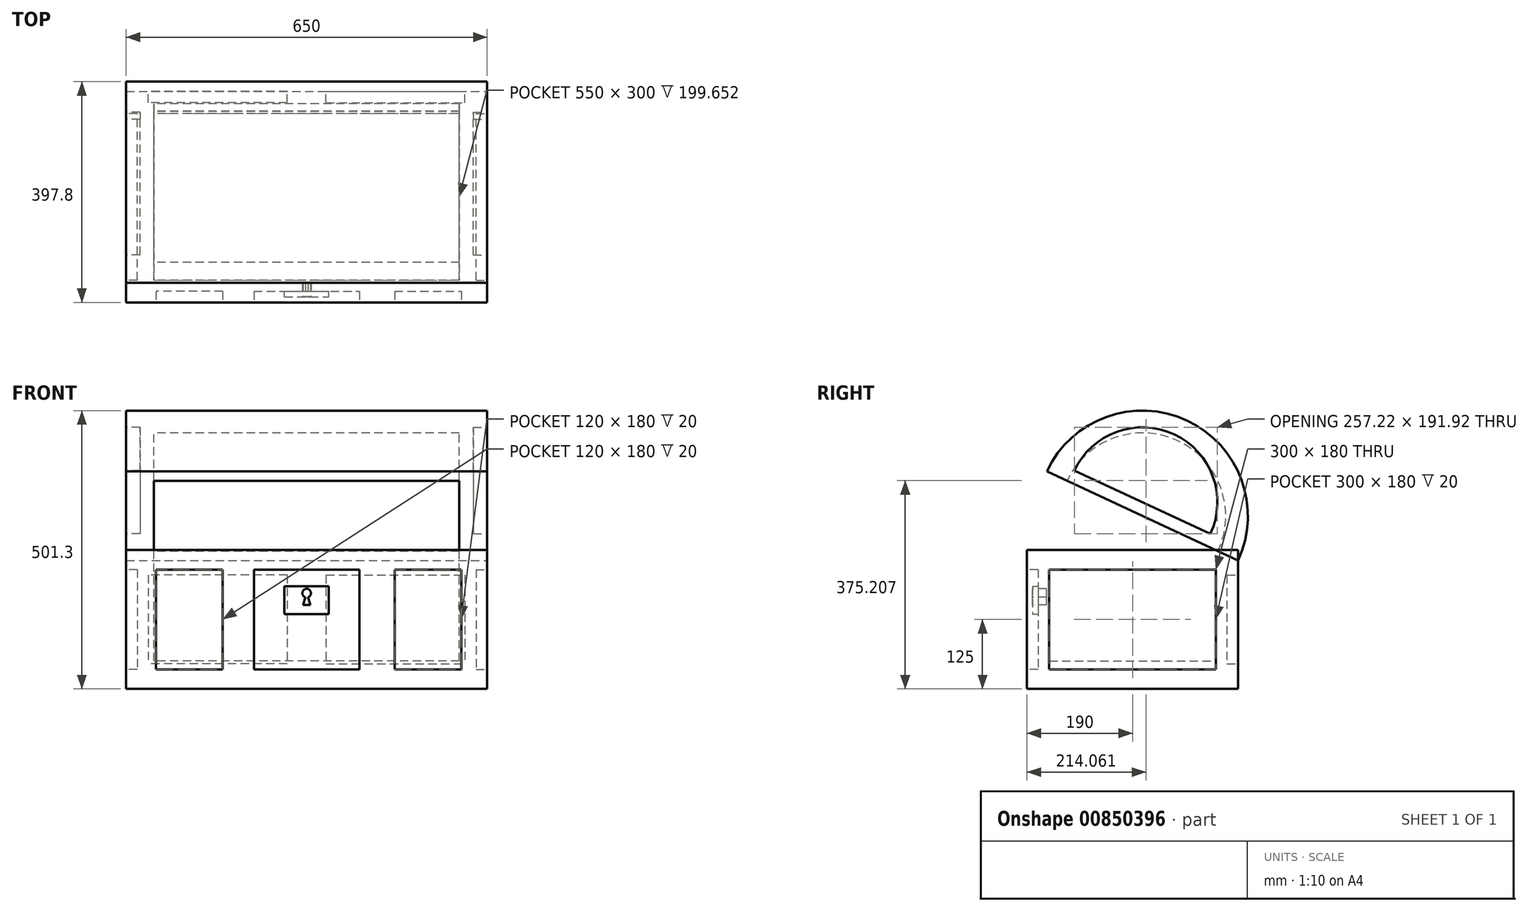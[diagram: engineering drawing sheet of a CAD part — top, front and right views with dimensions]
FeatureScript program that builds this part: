
annotation { "Feature Type Name" : "Feature", "Feature Type Description" : "" }
export const myFeature = defineFeature(function(context is Context, id is Id, definition is map)
    precondition{}
    {
        {
            var Q0;
            Q0=qCreatedBy(makeId("Top.planeOp"),FACE);
            var sketch = newSketch(context, id + "F0", { "sketchPlane" : qUnion([Q0])});
            skLineSegment(sketch, "E0.bottom", {"start": v(-32.5, 19) * mm, "end": v(32.5, 19) * mm});
            skLineSegment(sketch, "E0.top", {"start": v(-32.5, -19) * mm, "end": v(32.5, -19) * mm});
            skLineSegment(sketch, "E0.left", {"start": v(-32.5, 19) * mm, "end": v(-32.5, -19) * mm});
            skLineSegment(sketch, "E0.right", {"start": v(32.5, 19) * mm, "end": v(32.5, -19) * mm});
            skPoint(sketch, "E0.middle", {"position": v(0, 0) * mm});
            skSolve(sketch);
        }
        {
            var Q0;
            Q0=qSketchRegion(id+"F0",true);
            extrude(context, id + "F1", {"entities" : qUnion([Q0]), "depth" : 25 * mm, "offsetDistance" : 25 * mm});
        }
        {
            var Q0;
            Q0=qCreatedBy(makeId("Right.planeOp"),FACE);
            var sketch = newSketch(context, id + "F2", { "sketchPlane" : qUnion([Q0])});
            skArc(sketch, "E1", {"start": v(-19, 23.1) * mm, "mid": v(-9.8, 48.35) * mm, "end": v(15.44, 39.16) * mm});
            skLineSegment(sketch, "E2", {"start": v(15.44, 39.16) * mm, "end": v(-19, 23.1) * mm});
            skSolve(sketch);
        }
        {
            var Q0;
            Q0=qSketchRegion(id+"F2",true);
            extrude(context, id + "F3", {"entities" : qUnion([Q0]), "endBound" : BoundingType.SYMMETRIC, "depth" : 65 * mm, "offsetDistance" : 25 * mm});
        }
        {
            var Q0;
            Q0=qCreatedBy(makeId("Right.planeOp"),FACE);
            var sketch = newSketch(context, id + "F4", { "sketchPlane" : qUnion([Q0])});
            skArc(sketch, "E3", {"start": v(-15.37, 24.8) * mm, "mid": v(-8.12, 44.72) * mm, "end": v(11.81, 37.47) * mm});
            skLineSegment(sketch, "E4", {"start": v(11.81, 37.47) * mm, "end": v(-15.37, 24.8) * mm});
            skSolve(sketch);
        }
        {
            var Q0;
            Q0=qSketchRegion(id+"F4",true);
            extrude(context, id + "F5", {"entities" : qUnion([Q0]), "operationType" : NewBodyOperationType.REMOVE, "endBound" : BoundingType.SYMMETRIC, "oppositeDirection" : true, "depth" : 55 * mm, "offsetDistance" : 25 * mm});
        }
        {
            var Q0;
            Q0=makeQuery(id+"F3.opExtrude","CAP_FACE",FACE,{"disambiguationData":[OSD([sQuery(id+"F2.wireOp",EDGE,"E1"),sQuery(id+"F2.wireOp",EDGE,"E2")])],"isStart":false});
            var sketch = newSketch(context, id + "F6", { "sketchPlane" : qUnion([Q0])});
            skArc(sketch, "E5", {"start": v(-14.02, 25.42) * mm, "mid": v(-7.49, 43.36) * mm, "end": v(10.46, 36.84) * mm});
            skLineSegment(sketch, "E6", {"start": v(-14.02, 25.42) * mm, "end": v(10.46, 36.84) * mm});
            skSolve(sketch);
        }
        {
            var Q0;
            Q0=qSketchRegion(id+"F6",true);
            extrude(context, id + "F7", {"entities" : qUnion([Q0]), "oppositeDirection" : true, "depth" : 2.5 * mm, "offsetDistance" : 25 * mm});
        }
        {
            var Q0;
            Q0=makeQuery(id+"F7.opExtrude","SWEPT_BODY",BODY,{"disambiguationData":[OSD([sQuery(id+"F6.wireOp",EDGE,"E5"),sQuery(id+"F6.wireOp",EDGE,"E6")])]});
            transform(context, id + "F8", {"entities" : qUnion([Q0]), "transformType" : TransformType.TRANSLATION_3D, "dx" : 0 * mm, "dy" : 0 * mm, "dz" : 2.5 * mm, "makeCopy" : false});
        }
        {
            var Q0;
            Q0=makeQuery(id+"F7.opExtrude","SWEPT_BODY",BODY,{"disambiguationData":[OSD([sQuery(id+"F6.wireOp",EDGE,"E5"),sQuery(id+"F6.wireOp",EDGE,"E6")])]});
            var Q1;
            Q1=qCreatedBy(makeId("Right.planeOp"),FACE);
            mirror(context, id + "F9", {"entities" : qUnion([Q0]), "mirrorPlane" : qUnion([Q1])});
        }
        {
            var Q0;
            Q0=makeQuery(id+"F9.opPattern","COPY",BODY,{"derivedFrom":makeQuery(id+"F7.opExtrude","SWEPT_BODY",BODY,{"disambiguationData":[OSD([sQuery(id+"F6.wireOp",EDGE,"E5"),sQuery(id+"F6.wireOp",EDGE,"E6")])]}),"instanceName":"1"});
            var Q1;
            Q1=makeQuery(id+"F7.opExtrude","SWEPT_BODY",BODY,{"disambiguationData":[OSD([sQuery(id+"F6.wireOp",EDGE,"E5"),sQuery(id+"F6.wireOp",EDGE,"E6")])]});
            var Q2;
            Q2=makeQuery(id+"F3.opExtrude","SWEPT_BODY",BODY,{"disambiguationData":[OSD([sQuery(id+"F2.wireOp",EDGE,"E1"),sQuery(id+"F2.wireOp",EDGE,"E2")])]});
            booleanBodies(context, id + "F10", {"operationType" : BooleanOperationType.SUBTRACTION, "tools" : qUnion([Q0, Q1]), "targets" : qUnion([Q2])});
        }
        {
            var Q0;
            Q0=makeQuery(id+"F1.opExtrude","CAP_FACE",FACE,{"disambiguationData":[OSD([sQuery(id+"F0.wireOp",EDGE,"E0.bottom"),sQuery(id+"F0.wireOp",EDGE,"E0.top"),sQuery(id+"F0.wireOp",EDGE,"E0.left"),sQuery(id+"F0.wireOp",EDGE,"E0.right")])],"isStart":false});
            var sketch = newSketch(context, id + "F11", { "sketchPlane" : qUnion([Q0])});
            skLineSegment(sketch, "E7.bottom", {"start": v(-27.5, 15) * mm, "end": v(27.5, 15) * mm});
            skLineSegment(sketch, "E7.top", {"start": v(-27.5, -15) * mm, "end": v(27.5, -15) * mm});
            skLineSegment(sketch, "E7.left", {"start": v(-27.5, 15) * mm, "end": v(-27.5, -15) * mm});
            skLineSegment(sketch, "E7.right", {"start": v(27.5, 15) * mm, "end": v(27.5, -15) * mm});
            skPoint(sketch, "E7.middle", {"position": v(0, 0) * mm});
            skSolve(sketch);
        }
        {
            var Q0;
            Q0=qSketchRegion(id+"F11",true);
            extrude(context, id + "F12", {"entities" : qUnion([Q0]), "operationType" : NewBodyOperationType.REMOVE, "oppositeDirection" : true, "depth" : 20 * mm, "offsetDistance" : 25 * mm});
        }
        {
            var Q0;
            Q0=makeQuery(id+"F1.opExtrude","SWEPT_FACE",FACE,{"disambiguationData":[OSD([sQuery(id+"F0.wireOp",EDGE,"E0.left")])]});
            var sketch = newSketch(context, id + "F13", { "sketchPlane" : qUnion([Q0])});
            skPoint(sketch, "E8", {"position": v(0, 12.5) * mm});
            skPoint(sketch, "E8.positionSnap0", {"position": v(-19, 12.5) * mm});
            skPoint(sketch, "E8.positionSnap1", {"position": v(0, 25) * mm});
            skLineSegment(sketch, "E9.bottom", {"start": v(-15, 21.5) * mm, "end": v(15, 21.5) * mm});
            skLineSegment(sketch, "E9.top", {"start": v(-15, 3.5) * mm, "end": v(15, 3.5) * mm});
            skLineSegment(sketch, "E9.left", {"start": v(-15, 21.5) * mm, "end": v(-15, 3.5) * mm});
            skLineSegment(sketch, "E9.right", {"start": v(15, 21.5) * mm, "end": v(15, 3.5) * mm});
            skSolve(sketch);
        }
        {
            var Q0;
            Q0=qSketchRegion(id+"F13",true);
            extrude(context, id + "F14", {"entities" : qUnion([Q0]), "oppositeDirection" : true, "depth" : 2 * mm, "offsetDistance" : 25 * mm});
        }
        {
            var Q0;
            Q0=makeQuery(id+"F14.opExtrude","SWEPT_BODY",BODY,{"disambiguationData":[OSD([sQuery(id+"F13.wireOp",EDGE,"E9.bottom"),sQuery(id+"F13.wireOp",EDGE,"E9.top"),sQuery(id+"F13.wireOp",EDGE,"E9.left"),sQuery(id+"F13.wireOp",EDGE,"E9.right")])]});
            var Q1;
            Q1=qCreatedBy(makeId("Right.planeOp"),FACE);
            mirror(context, id + "F15", {"entities" : qUnion([Q0]), "mirrorPlane" : qUnion([Q1])});
        }
        {
            var Q0;
            Q0=makeQuery(id+"F15.opPattern","COPY",BODY,{"derivedFrom":makeQuery(id+"F14.opExtrude","SWEPT_BODY",BODY,{"disambiguationData":[OSD([sQuery(id+"F13.wireOp",EDGE,"E9.bottom"),sQuery(id+"F13.wireOp",EDGE,"E9.top"),sQuery(id+"F13.wireOp",EDGE,"E9.left"),sQuery(id+"F13.wireOp",EDGE,"E9.right")])]}),"instanceName":"1"});
            var Q1;
            Q1=makeQuery(id+"F14.opExtrude","SWEPT_BODY",BODY,{"disambiguationData":[OSD([sQuery(id+"F13.wireOp",EDGE,"E9.bottom"),sQuery(id+"F13.wireOp",EDGE,"E9.top"),sQuery(id+"F13.wireOp",EDGE,"E9.left"),sQuery(id+"F13.wireOp",EDGE,"E9.right")])]});
            var Q2;
            Q2=makeQuery(id+"F1.opExtrude","SWEPT_BODY",BODY,{"disambiguationData":[OSD([sQuery(id+"F0.wireOp",EDGE,"E0.bottom"),sQuery(id+"F0.wireOp",EDGE,"E0.top"),sQuery(id+"F0.wireOp",EDGE,"E0.left"),sQuery(id+"F0.wireOp",EDGE,"E0.right")])]});
            booleanBodies(context, id + "F16", {"operationType" : BooleanOperationType.SUBTRACTION, "tools" : qUnion([Q0, Q1]), "targets" : qUnion([Q2])});
        }
        {
            var Q0;
            Q0=makeQuery(id+"F1.opExtrude","SWEPT_FACE",FACE,{"disambiguationData":[OSD([sQuery(id+"F0.wireOp",EDGE,"E0.bottom")])]});
            var sketch = newSketch(context, id + "F17", { "sketchPlane" : qUnion([Q0])});
            skLineSegment(sketch, "E10.bottom", {"start": v(-9.5, 21.5) * mm, "end": v(9.5, 21.5) * mm});
            skLineSegment(sketch, "E10.top", {"start": v(-9.5, 3.5) * mm, "end": v(9.5, 3.5) * mm});
            skLineSegment(sketch, "E10.left", {"start": v(-9.5, 21.5) * mm, "end": v(-9.5, 3.5) * mm});
            skLineSegment(sketch, "E10.right", {"start": v(9.5, 21.5) * mm, "end": v(9.5, 3.5) * mm});
            skPoint(sketch, "E10.middle", {"position": v(0, 12.5) * mm});
            skPoint(sketch, "E10.middle.positionSnap0", {"position": v(-32.5, 12.5) * mm});
            skPoint(sketch, "E10.middle.positionSnap1", {"position": v(0, 25) * mm});
            skPoint(sketch, "E10.centerSnap0", {"position": v(-32.5, 12.5) * mm});
            skPoint(sketch, "E10.centerSnap1", {"position": v(0, 25) * mm});
            skLineSegment(sketch, "E11.bottom", {"start": v(-15.1, 21.5) * mm, "end": v(-27.1, 21.5) * mm});
            skLineSegment(sketch, "E11.top", {"start": v(-15.1, 3.5) * mm, "end": v(-27.1, 3.5) * mm});
            skLineSegment(sketch, "E11.left", {"start": v(-15.1, 21.5) * mm, "end": v(-15.1, 3.5) * mm});
            skLineSegment(sketch, "E11.right", {"start": v(-27.1, 21.5) * mm, "end": v(-27.1, 3.5) * mm});
            skPoint(sketch, "E11.middle", {"position": v(-21.1, 12.5) * mm});
            skLineSegment(sketch, "E12.bottom", {"start": v(15.85, 21.5) * mm, "end": v(27.85, 21.5) * mm});
            skLineSegment(sketch, "E12.top", {"start": v(15.85, 3.5) * mm, "end": v(27.85, 3.5) * mm});
            skLineSegment(sketch, "E12.left", {"start": v(15.85, 21.5) * mm, "end": v(15.85, 3.5) * mm});
            skLineSegment(sketch, "E12.right", {"start": v(27.85, 21.5) * mm, "end": v(27.85, 3.5) * mm});
            skPoint(sketch, "E12.middle", {"position": v(21.85, 12.5) * mm});
            skPoint(sketch, "E12.middle.positionSnap0", {"position": v(32.5, 12.5) * mm});
            skPoint(sketch, "E12.cornerSnap0", {"position": v(-21.1, 21.5) * mm});
            skPoint(sketch, "E12.centerSnap0", {"position": v(32.5, 12.5) * mm});
            skSolve(sketch);
        }
        {
            var Q0;
            Q0=makeQuery(id+"F17.imprint","IMPRINT",FACE,{"disambiguationData":[TD([[makeQuery(id+"F17.imprint","IMPRINT",EDGE,{"derivedFrom":sQuery(id+"F17.wireOp",EDGE,"E11.bottom")}),1.0]])]});
            var Q1;
            Q1=makeQuery(id+"F17.imprint","IMPRINT",FACE,{"disambiguationData":[TD([[makeQuery(id+"F17.imprint","IMPRINT",EDGE,{"derivedFrom":sQuery(id+"F17.wireOp",EDGE,"E10.bottom")}),-1.0]])]});
            var Q2;
            Q2=makeQuery(id+"F17.imprint","IMPRINT",FACE,{"disambiguationData":[TD([[makeQuery(id+"F17.imprint","IMPRINT",EDGE,{"derivedFrom":sQuery(id+"F17.wireOp",EDGE,"E12.bottom")}),-1.0]])]});
            extrude(context, id + "F18", {"entities" : qUnion([Q0, Q1, Q2]), "operationType" : NewBodyOperationType.REMOVE, "oppositeDirection" : true, "depth" : 2 * mm, "offsetDistance" : 25 * mm});
        }
        {
            var Q0;
            Q0=makeQuery(id+"F1.opExtrude","SWEPT_FACE",FACE,{"disambiguationData":[OSD([sQuery(id+"F0.wireOp",EDGE,"E0.top")])]});
            var sketch = newSketch(context, id + "F19", { "sketchPlane" : qUnion([Q0])});
            skLineSegment(sketch, "E13.bottom", {"start": v(-3.5, 20.5) * mm, "end": v(-28.5, 20.5) * mm});
            skLineSegment(sketch, "E13.top", {"start": v(-3.5, 4.5) * mm, "end": v(-28.5, 4.5) * mm});
            skLineSegment(sketch, "E13.left", {"start": v(-3.5, 20.5) * mm, "end": v(-3.5, 4.5) * mm});
            skLineSegment(sketch, "E13.right", {"start": v(-28.5, 20.5) * mm, "end": v(-28.5, 4.5) * mm});
            skPoint(sketch, "E13.middle", {"position": v(-16, 12.5) * mm});
            skPoint(sketch, "E13.middle.positionSnap0", {"position": v(-32.5, 12.5) * mm});
            skPoint(sketch, "E13.centerSnap0", {"position": v(-32.5, 12.5) * mm});
            skLineSegment(sketch, "E14.bottom", {"start": v(3.5, 20.5) * mm, "end": v(28.5, 20.5) * mm});
            skLineSegment(sketch, "E14.top", {"start": v(3.5, 4.5) * mm, "end": v(28.5, 4.5) * mm});
            skLineSegment(sketch, "E14.left", {"start": v(3.5, 20.5) * mm, "end": v(3.5, 4.5) * mm});
            skLineSegment(sketch, "E14.right", {"start": v(28.5, 20.5) * mm, "end": v(28.5, 4.5) * mm});
            skPoint(sketch, "E14.middle", {"position": v(16, 12.5) * mm});
            skSolve(sketch);
        }
        {
            var Q0;
            Q0=makeQuery(id+"F19.imprint","IMPRINT",FACE,{"disambiguationData":[TD([[makeQuery(id+"F19.imprint","IMPRINT",EDGE,{"derivedFrom":sQuery(id+"F19.wireOp",EDGE,"E13.bottom")}),1.0]])]});
            var Q1;
            Q1=makeQuery(id+"F19.imprint","IMPRINT",FACE,{"disambiguationData":[TD([[makeQuery(id+"F19.imprint","IMPRINT",EDGE,{"derivedFrom":sQuery(id+"F19.wireOp",EDGE,"E14.bottom")}),-1.0]])]});
            extrude(context, id + "F20", {"entities" : qUnion([Q0, Q1]), "operationType" : NewBodyOperationType.REMOVE, "oppositeDirection" : true, "depth" : 2 * mm, "offsetDistance" : 25 * mm});
        }
        {
            var Q0;
            Q0=makeQuery(id+"F18.boolean.opBoolean","COPY",FACE,{"derivedFrom":makeQuery(id+"F18.opExtrude","CAP_FACE",FACE,{"disambiguationData":[OSD([sQuery(id+"F17.wireOp",EDGE,"E10.bottom"),sQuery(id+"F17.wireOp",EDGE,"E10.top"),sQuery(id+"F17.wireOp",EDGE,"E10.left"),sQuery(id+"F17.wireOp",EDGE,"E10.right")])],"isStart":false})});
            var sketch = newSketch(context, id + "F21", { "sketchPlane" : qUnion([Q0])});
            skLineSegment(sketch, "E15.bottom", {"start": v(-4, 18.47) * mm, "end": v(4, 18.47) * mm});
            skLineSegment(sketch, "E15.top", {"start": v(-4, 13.47) * mm, "end": v(4, 13.47) * mm});
            skLineSegment(sketch, "E15.left", {"start": v(-4, 18.47) * mm, "end": v(-4, 13.47) * mm});
            skLineSegment(sketch, "E15.right", {"start": v(4, 18.47) * mm, "end": v(4, 13.47) * mm});
            skPoint(sketch, "E15.middle", {"position": v(0, 15.97) * mm});
            skSolve(sketch);
        }
        {
            var Q0;
            Q0=qSketchRegion(id+"F21",true);
            extrude(context, id + "F22", {"entities" : qUnion([Q0]), "operationType" : NewBodyOperationType.ADD, "depth" : 1 * mm, "offsetDistance" : 25 * mm});
        }
        {
            var Q0;
            Q0=makeQuery(id+"F22.opExtrude","CAP_FACE",FACE,{"disambiguationData":[OSD([sQuery(id+"F21.wireOp",EDGE,"E15.bottom"),sQuery(id+"F21.wireOp",EDGE,"E15.top"),sQuery(id+"F21.wireOp",EDGE,"E15.left"),sQuery(id+"F21.wireOp",EDGE,"E15.right")])],"isStart":false});
            var sketch = newSketch(context, id + "F23", { "sketchPlane" : qUnion([Q0])});
            skCircle(sketch, "E16", {"center": v(0, 17.24) * mm, "radius": 0.78 * mm});
            skLineSegment(sketch, "E17", {"start": v(0, 15.12) * mm, "end": v(-0.65, 15.12) * mm});
            skLineSegment(sketch, "E18", {"start": v(-0.65, 15.12) * mm, "end": v(0, 17.24) * mm});
            skLineSegment(sketch, "E19.MirrorCS", {"start": v(0.65, 15.12) * mm, "end": v(0, 17.24) * mm});
            skLineSegment(sketch, "E20.MirrorCS", {"start": v(0, 15.12) * mm, "end": v(0.65, 15.12) * mm});
            skSolve(sketch);
        }
        {
            var Q0;
            Q0=qSketchRegion(id+"F23",true);
            extrude(context, id + "F24", {"entities" : qUnion([Q0]), "operationType" : NewBodyOperationType.REMOVE, "oppositeDirection" : true, "depth" : 2.5 * mm, "offsetDistance" : 25 * mm});
        }
        {
            var Q0;
            Q0=makeQuery(id+"F1.opExtrude","SWEPT_BODY",BODY,{"disambiguationData":[OSD([sQuery(id+"F0.wireOp",EDGE,"E0.bottom"),sQuery(id+"F0.wireOp",EDGE,"E0.top"),sQuery(id+"F0.wireOp",EDGE,"E0.left"),sQuery(id+"F0.wireOp",EDGE,"E0.right")])]});
            var Q1;
            Q1=makeQuery(id+"F3.opExtrude","SWEPT_BODY",BODY,{"disambiguationData":[OSD([sQuery(id+"F2.wireOp",EDGE,"E1"),sQuery(id+"F2.wireOp",EDGE,"E2")])]});
            var Q2;
            Q2=makeQuery(id+"F1.opExtrude","SWEPT_EDGE",EDGE,{"disambiguationData":[OSD([sQuery(id+"F0.wireOp",EDGE,"E0.top"),sQuery(id+"F0.wireOp",EDGE,"E0.right")])]});
            transform(context, id + "F25", {"entities" : qUnion([Q0, Q1]), "transformType" : TransformType.ROTATION, "transformAxis" : qUnion([Q2]), "angle" : 180 * degree, "makeCopy" : false});
        }
        {
            var Q0;
            Q0=makeQuery(id+"F3.opExtrude","SWEPT_BODY",BODY,{"disambiguationData":[OSD([sQuery(id+"F2.wireOp",EDGE,"E1"),sQuery(id+"F2.wireOp",EDGE,"E2")])]});
            var Q1;
            Q1=makeQuery(id+"F1.opExtrude","SWEPT_BODY",BODY,{"disambiguationData":[OSD([sQuery(id+"F0.wireOp",EDGE,"E0.bottom"),sQuery(id+"F0.wireOp",EDGE,"E0.top"),sQuery(id+"F0.wireOp",EDGE,"E0.left"),sQuery(id+"F0.wireOp",EDGE,"E0.right")])]});
            transform(context, id + "F26", {"entities" : qUnion([Q0, Q1]), "transformType" : TransformType.TRANSLATION_3D, "dx" : -65 * mm, "dy" : 38 * mm, "dz" : 0 * mm, "makeCopy" : false});
        }
        {
            var Q0;
            Q0=makeQuery(id+"F3.opExtrude","SWEPT_BODY",BODY,{"disambiguationData":[OSD([sQuery(id+"F2.wireOp",EDGE,"E1"),sQuery(id+"F2.wireOp",EDGE,"E2")])]});
            var Q1;
            Q1=makeQuery(id+"F1.opExtrude","SWEPT_BODY",BODY,{"disambiguationData":[OSD([sQuery(id+"F0.wireOp",EDGE,"E0.bottom"),sQuery(id+"F0.wireOp",EDGE,"E0.top"),sQuery(id+"F0.wireOp",EDGE,"E0.left"),sQuery(id+"F0.wireOp",EDGE,"E0.right")])]});
            var Q2;
            Q2=qCreatedBy(makeId("Origin.pointOp"),VERTEX);
            transform(context, id + "F27", {"entities" : qUnion([Q0, Q1]), "transformType" : TransformType.SCALE_UNIFORMLY, "scale" : 10, "scalePoint" : qUnion([Q2]), "makeCopy" : false});
        }
    });
